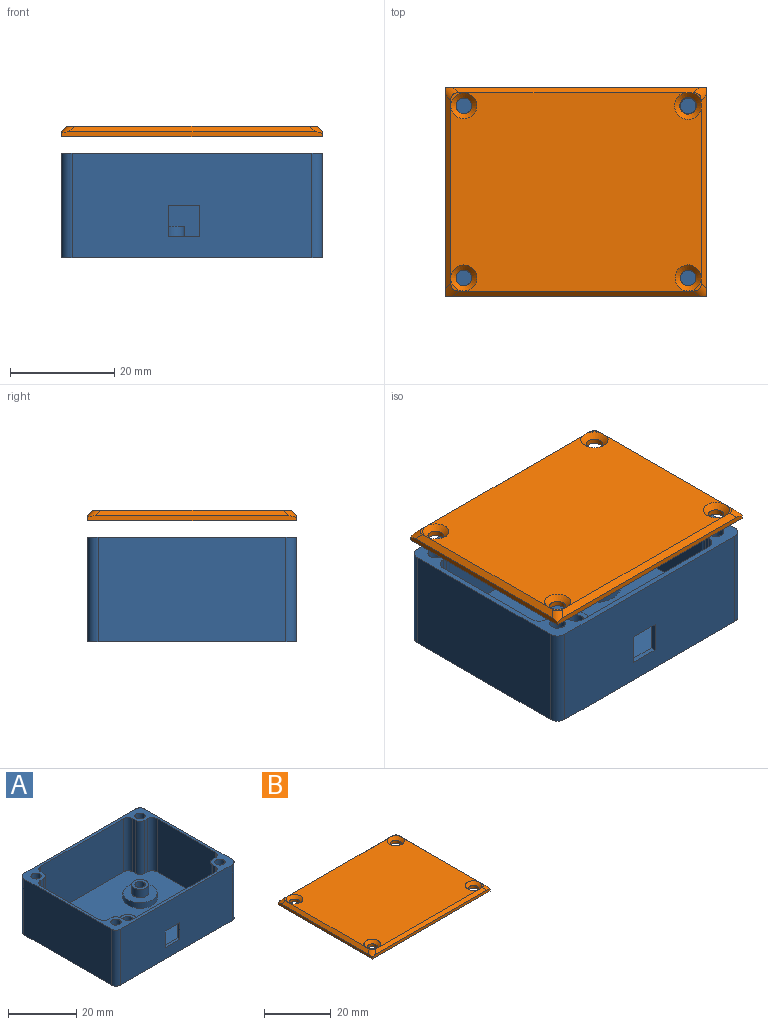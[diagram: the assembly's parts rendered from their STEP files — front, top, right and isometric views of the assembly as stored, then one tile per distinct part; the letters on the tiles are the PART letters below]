
ASSEMBLY  parts=2 mates=1
PART A: 71 faces, bbox 50x40x20 mm
  f0: plane 34x19mm, normal (0,1,0), area 610.5mm2, adj f4,f8,f55,f57,f67,f68,f69,f70
  f1: plane 46x20mm, normal (0,-1,0), area 884.5mm2, adj f8,f12,f52,f66,f67,f68,f69,f70
  f2: cylinder r=1.5mm len=4mm, axis (0,0,-1), area 37.7mm2, adj f30,f50
  f3: cylinder r=1.5mm len=4mm, axis (0,0,-1), area 37.7mm2, adj f32,f43
  f4: plane 48x38mm, normal (0,0,1), area 1563.5mm2, adj f0,f5,f6,f7,f13,f14,f15,f16
  f5: plane 24x19mm, normal (1,0,0), area 456mm2, adj f4,f8,f56,f65
  f6: plane 24x19mm, normal (-1,0,0), area 456mm2, adj f4,f8,f59,f60
  f7: plane 34x19mm, normal (0,-1,0), area 646mm2, adj f4,f8,f61,f63
  f8: plane 50x40mm, normal (0,0,1), area 247.7mm2, adj f0,f1,f5,f6,f7,f9,f10,f11
  f9: plane 46x20mm, normal (0,1,0), area 920mm2, adj f8,f12,f51,f53
  f10: plane 36x20mm, normal (-1,0,0), area 720mm2, adj f8,f12,f51,f66
  f11: plane 36x20mm, normal (1,0,0), area 720mm2, adj f8,f12,f52,f53
  f12: plane 50x40mm, normal (0,0,-1), area 1949.8mm2, adj f1,f9,f10,f11,f37,f38,f39,f40
  f13: plane 19x1mm, normal (0,-1,0), area 19mm2, adj f4,f8,f60,f62
  f14: plane 19x1mm, normal (-1,0,0), area 19mm2, adj f4,f8,f61,f62
  f15: plane 19x1mm, normal (0,1,0), area 19mm2, adj f4,f8,f58,f59
  f16: plane 19x1mm, normal (-1,0,0), area 19mm2, adj f4,f8,f57,f58
  f17: plane 19x1mm, normal (0,1,0), area 19mm2, adj f4,f8,f54,f56
  f18: plane 19x1mm, normal (1,0,0), area 19mm2, adj f4,f8,f54,f55
  f19: plane 19x1mm, normal (0,-1,0), area 19mm2, adj f4,f8,f64,f65
  f20: plane 19x1mm, normal (1,0,0), area 19mm2, adj f4,f8,f63,f64
  f21: cylinder r=1.5mm len=10mm, axis (0,0,1), area 94.2mm2, adj f8,f22
  f22: plane 3x3mm, normal (0,0,1), area 7.1mm2, adj f21
  f23: cylinder r=1.5mm len=10mm, axis (0,0,1), area 94.2mm2, adj f8,f24
  f24: plane 3x3mm, normal (0,0,1), area 7.1mm2, adj f23
  f25: cylinder r=1.5mm len=10mm, axis (0,0,1), area 94.2mm2, adj f8,f26
  f26: plane 3x3mm, normal (0,0,1), area 7.1mm2, adj f25
  f27: cylinder r=1.5mm len=10mm, axis (0,0,1), area 94.2mm2, adj f8,f28
  f28: plane 3x3mm, normal (0,0,1), area 7.1mm2, adj f27
  f29: cylinder r=2.5mm len=5mm, axis (0,0,-1), area 47.1mm2, adj f30,f36
  f30: plane 5x5mm, normal (0,0,1), area 12.6mm2, adj f2,f29
  f31: cylinder r=2.5mm len=5mm, axis (0,0,-1), area 47.1mm2, adj f32,f34
  f32: plane 5x5mm, normal (0,0,1), area 12.6mm2, adj f3,f31
  f33: cylinder r=5mm len=10mm, axis (0,0,-1), area 62.8mm2, adj f4,f34
  f34: plane 10x10mm, normal (0,0,1), area 58.9mm2, adj f31,f33
  f35: cylinder r=5mm len=10mm, axis (0,0,-1), area 62.8mm2, adj f4,f36
  f36: plane 10x10mm, normal (0,0,1), area 58.9mm2, adj f29,f35
  f37: plane 2.83x2mm, normal (0.94,0.33,0), area 6mm2, adj f12,f38,f42,f43
  f38: plane 2.28x2mm, normal (0.76,-0.65,0), area 6mm2, adj f12,f37,f39,f43
  f39: plane 2.95x2mm, normal (-0.18,-0.98,0), area 6mm2, adj f12,f38,f40,f43
  f40: plane 2.83x2mm, normal (-0.94,-0.33,0), area 6mm2, adj f12,f39,f41,f43
  f41: plane 2.28x2mm, normal (-0.76,0.65,0), area 6mm2, adj f12,f40,f42,f43
  f42: plane 2.95x2mm, normal (0.18,0.98,0), area 6mm2, adj f12,f37,f41,f43
  f43: plane 5.9x5.66mm, normal (0,0,-1), area 16.3mm2, adj f3,f37,f38,f39,f40,f41,f42
  f44: plane 2.86x2mm, normal (0.95,0.3,0), area 6mm2, adj f12,f45,f49,f50
  f45: plane 2.22x2.02mm, normal (0.74,-0.67,0), area 6mm2, adj f12,f44,f46,f50
  f46: plane 2.93x2mm, normal (-0.21,-0.98,0), area 6mm2, adj f12,f45,f47,f50
  f47: plane 2.86x2mm, normal (-0.95,-0.3,0), area 6mm2, adj f12,f46,f48,f50
  f48: plane 2.22x2.02mm, normal (-0.74,0.67,0), area 6mm2, adj f12,f47,f49,f50
  f49: plane 2.93x2mm, normal (0.21,0.98,0), area 6mm2, adj f12,f44,f48,f50
  f50: plane 5.86x5.72mm, normal (0,0,-1), area 16.3mm2, adj f2,f44,f45,f46,f47,f48,f49
  f51: cylinder r=2mm len=20mm, axis (0,0,1), area 62.8mm2, adj f8,f9,f10,f12
  f52: cylinder r=2mm len=20mm, axis (0,0,1), area 62.8mm2, adj f1,f8,f11,f12
  f53: cylinder r=2mm len=20mm, axis (0,0,-1), area 62.8mm2, adj f8,f9,f11,f12
  f54: cylinder r=2mm len=19mm, axis (0,0,1), area 59.7mm2, adj f4,f8,f17,f18
  f55: cylinder r=2mm len=19mm, axis (0,0,-1), area 59.7mm2, adj f0,f4,f8,f18
  f56: cylinder r=2mm len=19mm, axis (0,0,1), area 59.7mm2, adj f4,f5,f8,f17
  f57: cylinder r=2mm len=19mm, axis (0,0,1), area 59.7mm2, adj f0,f4,f8,f16
  f58: cylinder r=2mm len=19mm, axis (0,0,1), area 59.7mm2, adj f4,f8,f15,f16
  f59: cylinder r=2mm len=19mm, axis (0,0,1), area 59.7mm2, adj f4,f6,f8,f15
  f60: cylinder r=2mm len=19mm, axis (0,0,-1), area 59.7mm2, adj f4,f6,f8,f13
  f61: cylinder r=2mm len=19mm, axis (0,0,1), area 59.7mm2, adj f4,f7,f8,f14
  f62: cylinder r=2mm len=19mm, axis (0,0,1), area 59.7mm2, adj f4,f8,f13,f14
  f63: cylinder r=2mm len=19mm, axis (0,0,-1), area 59.7mm2, adj f4,f7,f8,f20
  f64: cylinder r=2mm len=19mm, axis (0,0,1), area 59.7mm2, adj f4,f8,f19,f20
  f65: cylinder r=2mm len=19mm, axis (0,0,-1), area 59.7mm2, adj f4,f5,f8,f19
  f66: cylinder r=2mm len=20mm, axis (0,0,-1), area 62.8mm2, adj f1,f8,f10,f12
  f67: plane 5.95x1mm, normal (0,0,-1), area 5.9mm2, adj f0,f1,f68,f70
  f68: plane 5.98x1mm, normal (1,0,0), area 6mm2, adj f0,f1,f67,f69
  f69: plane 5.95x1mm, normal (0,0,1), area 5.9mm2, adj f0,f1,f68,f70
  f70: plane 5.98x1mm, normal (-1,0,0), area 6mm2, adj f0,f1,f67,f69
PART B: 26 faces, bbox 51.2x41.2x2.2 mm
  f0: plane 1.77x1.77mm, normal (0,0,1), area 0.7mm2, adj f18,f19,f20,f24
  f1: plane 2.5x2.5mm, normal (0,0,1), area 1mm2, adj f14,f16,f17,f22
  f2: plane 2.5x2.5mm, normal (0,0,1), area 1mm2, adj f16,f18,f21,f23
  f3: plane 48x38mm, normal (0,0,1), area 1738.9mm2, adj f14,f15,f16,f17,f18,f19,f20,f21
  f4: plane 40x1mm, normal (-1,0,0), area 39.6mm2, adj f5,f7,f9,f16,f22,f23
  f5: plane 50x1mm, normal (0,-1,0), area 49.6mm2, adj f4,f6,f9,f17,f22,f25
  f6: plane 40x1mm, normal (1,0,0), area 39.6mm2, adj f5,f7,f9,f19,f24,f25
  f7: plane 50x1mm, normal (0,1,0), area 49.6mm2, adj f4,f6,f9,f18,f23,f24
  f8: plane 2.5x2.5mm, normal (0,0,1), area 1mm2, adj f15,f17,f19,f25
  f9: plane 50x40mm, normal (0,0,-1), area 1970.7mm2, adj f4,f5,f6,f7,f10,f11,f12,f13
  f10: cylinder r=1.5mm len=3mm, axis (0,0,1), area 9.4mm2, adj f9,f21
  f11: cylinder r=1.6mm len=3.21mm, axis (0,0,1), area 10.1mm2, adj f9,f20
  f12: cylinder r=1.5mm len=3mm, axis (0,0,1), area 9.4mm2, adj f9,f15
  f13: cylinder r=1.5mm len=3mm, axis (0,0,1), area 9.4mm2, adj f9,f14
  f14: cone r=1.5mm half-angle=45deg, axis (0,0,1), area 17.8mm2, adj f1,f3,f13
  f15: cone r=1.5mm half-angle=45deg, axis (0,0,1), area 17.8mm2, adj f3,f8,f12
  f16: plane 37.17x1mm, normal (-0.71,0,0.71), area 51.2mm2, adj f1,f2,f3,f4,f22,f23
  f17: plane 47.17x1mm, normal (0,-0.71,0.71), area 65.3mm2, adj f1,f3,f5,f8,f22,f25
  f18: plane 47.17x1mm, normal (0,0.71,0.71), area 65.2mm2, adj f0,f2,f3,f7,f20,f23,f24
  f19: plane 37.17x1mm, normal (0.71,0,0.71), area 51.1mm2, adj f0,f3,f6,f8,f20,f24,f25
  f20: cone r=1.6mm half-angle=45deg, axis (0,0,1), area 18.6mm2, adj f0,f3,f11,f18,f19
  f21: cone r=1.5mm half-angle=45deg, axis (0,0,1), area 17.8mm2, adj f2,f3,f10
  f22: cylinder r=2mm len=3.01mm, axis (0.58,0.58,0.58), area 4.1mm2, adj f1,f4,f5,f16,f17
  f23: cylinder r=2mm len=3.01mm, axis (0.58,-0.58,0.58), area 4.1mm2, adj f2,f4,f7,f16,f18
  f24: cylinder r=2mm len=3.01mm, axis (0.58,0.58,-0.58), area 4.1mm2, adj f0,f6,f7,f18,f19
  f25: cylinder r=2mm len=3.01mm, axis (0.58,-0.58,-0.58), area 4.1mm2, adj f5,f6,f8,f17,f19
PLACE A t=(-67.84,-42.21,17.75)mm fixed
PLACE B t=(-152.07,-56.46,40.9)mm
MATE slider A.f27 <-> B.f13  axis (0,0,1) through (-124.7,-29.13,37.75)mm
